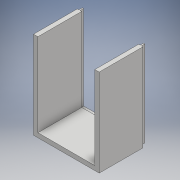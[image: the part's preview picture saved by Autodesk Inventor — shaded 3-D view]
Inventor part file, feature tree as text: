
AUTODESK INVENTOR PART (.ipt)
format: ipt  version: 2017 (Build 210142000, 142)  size: 160,768 bytes
history: native  units: mm
features: extrude x9, sketch x9
ambient origin geometry x8: Origin, YZ Plane, XZ Plane, XY Plane, X Axis, Y Axis, Z Axis, Center Point
bodies: Solid1 (feature_tree)
feature tree (18):
  extrude  "Extrusion1"  Depth=100.0mm
  extrude  "Extrusion2"  Depth=65.0mm
  extrude  "Extrusion3"  Depth=50.0mm TaperAngle=0.0deg
  extrude  "Extrusion4"  Depth=2.0mm
  extrude  "Extrusion5"  Depth=2.0mm
  extrude  "Extrusion6"  Depth=4.0mm TaperAngle=0.0deg
  extrude  "Extrusion7"  Depth=0.25mm TaperAngle=0.0deg
  extrude  "Extrusion8"  Depth=0.25mm TaperAngle=0.0deg
  extrude  "Extrusion9"  [1 undecoded]
  sketch  "Sketch1"  dims[d0=75.0mm d1=100.0mm]
  sketch  "Sketch2"  dims[d2=50.0mm d3=0.0mm d4=65.0mm]
  sketch  "Sketch3"  dims[d5=95.0mm d6=50.0mm d7=0.0mm]
  sketch  "Sketch4"  dims[d8=2.0mm d9=98.5mm]
  sketch  "Sketch5"  dims[d10=72.0mm d11=2.0mm]
  sketch  "Sketch6"  dims[d12=4.0mm d13=0.0mm d14=0.25mm d15=0.0mm]
  sketch  "Sketch7"  dims[d16=0.25mm d17=0.0mm d18=0.25mm d19=0.0mm]
  sketch  "Sketch8"  dims[d20=0.25mm d21=0.0mm d22=0.25mm d23=0.0mm]
  sketch  "Sketch9"  dims[d24=0.25mm d25=0.0mm]
note: 1 required parameter value undecoded (feature->parameter linkage not recoverable at this tier; creation-order binding heuristic only, values carry confidence <= 0.55)
